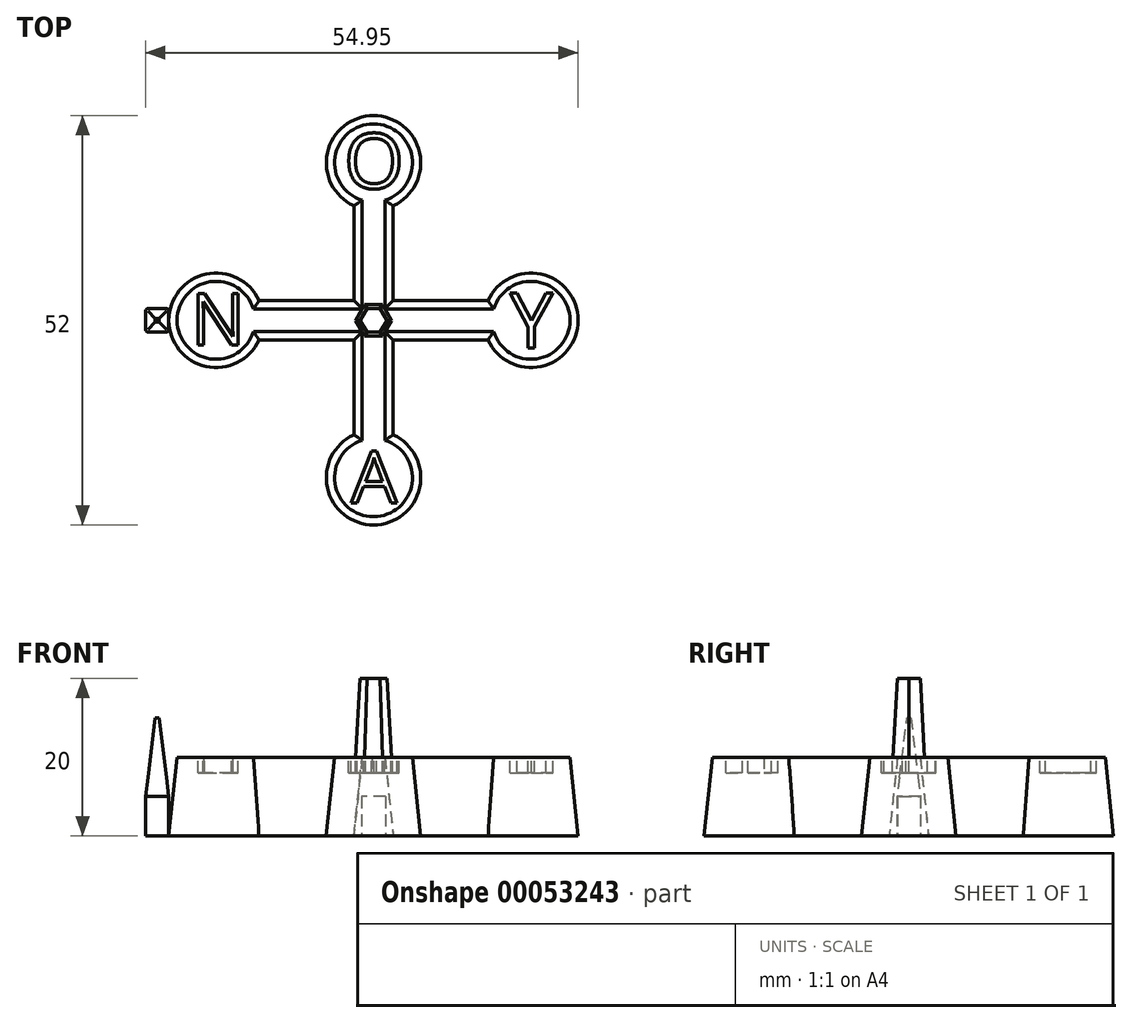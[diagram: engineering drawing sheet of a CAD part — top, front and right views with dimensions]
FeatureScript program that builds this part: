
annotation { "Feature Type Name" : "Feature", "Feature Type Description" : "" }
export const myFeature = defineFeature(function(context is Context, id is Id, definition is map)
    precondition{}
    {
        {
            var Q0;
            Q0=qCreatedBy(makeId("Top.planeOp"),FACE);
            var sketch = newSketch(context, id + "F0", { "sketchPlane" : qUnion([Q0])});
            skArc(sketch, "E0", {"start": v(-19.1, -5.93) * mm, "mid": v(20, 0) * mm, "end": v(-19.1, 5.93) * mm, "construction": true});
            skArc(sketch, "E1", {"start": v(2.5, 14.55) * mm, "mid": v(0, 26) * mm, "end": v(-2.5, 14.55) * mm});
            skArc(sketch, "E2", {"start": v(14.55, -2.5) * mm, "mid": v(26, 0) * mm, "end": v(14.55, 2.5) * mm});
            skArc(sketch, "E3", {"start": v(-2.5, -14.55) * mm, "mid": v(0, -26) * mm, "end": v(2.5, -14.55) * mm});
            skArc(sketch, "E4", {"start": v(-14.55, 2.5) * mm, "mid": v(-26, 0) * mm, "end": v(-14.55, -2.5) * mm});
            skLineSegment(sketch, "E5.rect.bottom", {"start": v(14.55, -2.5) * mm, "end": v(2.5, -2.5) * mm});
            skLineSegment(sketch, "E5.rect.top", {"start": v(14.55, 2.5) * mm, "end": v(2.5, 2.5) * mm});
            skLineSegment(sketch, "E6.rect.left", {"start": v(2.5, -14.55) * mm, "end": v(2.5, -2.5) * mm});
            skLineSegment(sketch, "E6.rect.right", {"start": v(-2.5, -14.55) * mm, "end": v(-2.5, -2.5) * mm});
            skLineSegment(sketch, "E7.trimOffspring", {"start": v(-2.5, 2.5) * mm, "end": v(-2.5, 14.55) * mm});
            skLineSegment(sketch, "E8.trimOffspring", {"start": v(-2.5, 2.5) * mm, "end": v(-14.55, 2.5) * mm});
            skLineSegment(sketch, "E9.trimOffspring", {"start": v(2.5, 2.5) * mm, "end": v(2.5, 14.55) * mm});
            skLineSegment(sketch, "E10.trimOffspring", {"start": v(-2.5, -2.5) * mm, "end": v(-14.55, -2.5) * mm});
            skSolve(sketch);
        }
        {
            var Q0;
            Q0 = qSketchRegion(id + "F0", true);
            extrude(context, id + "F1", {"entities" : qUnion([Q0]), "depth" : 10 * mm, "hasDraft" : true, "draftAngle" : 6 * degree, "draftPullDirection" : true});
        }
        {
            var Q0;
            Q0=makeQuery(id+"F1.opExtrude","CAP_FACE",FACE,{"disambiguationData":[OSD([sQuery(id+"F0.wireOp",EDGE,"E1"),sQuery(id+"F0.wireOp",EDGE,"E2"),sQuery(id+"F0.wireOp",EDGE,"E3"),sQuery(id+"F0.wireOp",EDGE,"E4"),sQuery(id+"F0.wireOp",EDGE,"E5.rect.bottom"),sQuery(id+"F0.wireOp",EDGE,"E5.rect.top"),sQuery(id+"F0.wireOp",EDGE,"E6.rect.left"),sQuery(id+"F0.wireOp",EDGE,"E6.rect.right"),sQuery(id+"F0.wireOp",EDGE,"E7.trimOffspring"),sQuery(id+"F0.wireOp",EDGE,"E8.trimOffspring"),sQuery(id+"F0.wireOp",EDGE,"E9.trimOffspring"),sQuery(id+"F0.wireOp",EDGE,"E10.trimOffspring")])],"isStart":false});
            var sketch = newSketch(context, id + "F2", { "sketchPlane" : qUnion([Q0])});
            skCircle(sketch, "E11.cCircle", {"center": v(0, 0) * mm, "radius": 2 * mm, "construction": true});
            skLineSegment(sketch, "E11.0", {"start": v(1.15, -2) * mm, "end": v(-1.15, -2) * mm});
            skLineSegment(sketch, "E11.1", {"start": v(-1.15, -2) * mm, "end": v(-2.3, 0) * mm});
            skLineSegment(sketch, "E11.2", {"start": v(-2.3, 0) * mm, "end": v(-1.15, 2) * mm});
            skLineSegment(sketch, "E11.3", {"start": v(-1.15, 2) * mm, "end": v(1.15, 2) * mm});
            skLineSegment(sketch, "E11.4", {"start": v(1.15, 2) * mm, "end": v(2.3, 0) * mm});
            skLineSegment(sketch, "E11.5", {"start": v(2.3, 0) * mm, "end": v(1.15, -2) * mm});
            skPoint(sketch, "E11.0.midPoint", {"position": v(0, -2) * mm});
            skSolve(sketch);
        }
        {
            var Q0;
            Q0 = qSketchRegion(id + "F2", true);
            extrude(context, id + "F3", {"entities" : qUnion([Q0]), "operationType" : NewBodyOperationType.ADD, "depth" : 10 * mm, "hasDraft" : true, "draftAngle" : 3 * degree, "draftPullDirection" : true});
        }
        {
            var Q0;
            Q0=makeQuery(id+"F1.opExtrude","CAP_FACE",FACE,{"disambiguationData":[OSD([sQuery(id+"F0.wireOp",EDGE,"E1"),sQuery(id+"F0.wireOp",EDGE,"E2"),sQuery(id+"F0.wireOp",EDGE,"E3"),sQuery(id+"F0.wireOp",EDGE,"E4"),sQuery(id+"F0.wireOp",EDGE,"E5.rect.bottom"),sQuery(id+"F0.wireOp",EDGE,"E5.rect.top"),sQuery(id+"F0.wireOp",EDGE,"E6.rect.left"),sQuery(id+"F0.wireOp",EDGE,"E6.rect.right"),sQuery(id+"F0.wireOp",EDGE,"E7.trimOffspring"),sQuery(id+"F0.wireOp",EDGE,"E8.trimOffspring"),sQuery(id+"F0.wireOp",EDGE,"E9.trimOffspring"),sQuery(id+"F0.wireOp",EDGE,"E10.trimOffspring")])],"isStart":true});
            var sketch = newSketch(context, id + "F4", { "sketchPlane" : qUnion([Q0])});
            skLineSegment(sketch, "E12.rect.bottom", {"start": v(1.5, -1.5) * mm, "end": v(-1.5, -1.5) * mm});
            skLineSegment(sketch, "E12.rect.top", {"start": v(1.5, 1.5) * mm, "end": v(-1.5, 1.5) * mm});
            skLineSegment(sketch, "E12.rect.left", {"start": v(1.5, -1.5) * mm, "end": v(1.5, 1.5) * mm});
            skLineSegment(sketch, "E12.rect.right", {"start": v(-1.5, -1.5) * mm, "end": v(-1.5, 1.5) * mm});
            skPoint(sketch, "E12.rect.middle", {"position": v(0, 0) * mm});
            skSolve(sketch);
        }
        {
            var Q0;
            Q0 = qSketchRegion(id + "F4", true);
            extrude(context, id + "F5", {"entities" : qUnion([Q0]), "operationType" : NewBodyOperationType.REMOVE, "oppositeDirection" : true, "depth" : 5 * mm});
        }
        {
            var Q0;
            Q0=qCreatedBy(makeId("Top.planeOp"),FACE);
            var sketch = newSketch(context, id + "F6", { "sketchPlane" : qUnion([Q0])});
            skLineSegment(sketch, "E13.rect.bottom", {"start": v(-26.3, -1.48) * mm, "end": v(-28.65, -1.48) * mm});
            skLineSegment(sketch, "E13.rect.top", {"start": v(-26.3, 1.47) * mm, "end": v(-28.65, 1.47) * mm});
            skLineSegment(sketch, "E13.rect.left", {"start": v(-26, -1.18) * mm, "end": v(-26, 1.17) * mm});
            skLineSegment(sketch, "E13.rect.right", {"start": v(-28.95, -1.18) * mm, "end": v(-28.95, 1.17) * mm});
            skPoint(sketch, "E13.rect.middle", {"position": v(-27.48, 0) * mm});
            skPoint(sketch, "E14.visualSharp", {"position": v(-28.95, 1.47) * mm});
            skArc(sketch, "E14.filletArc", {"start": v(-28.65, 1.47) * mm, "mid": v(-28.86, 1.39) * mm, "end": v(-28.95, 1.17) * mm});
            skPoint(sketch, "E15.visualSharp", {"position": v(-26, 1.47) * mm});
            skArc(sketch, "E15.filletArc", {"start": v(-26, 1.17) * mm, "mid": v(-26.09, 1.39) * mm, "end": v(-26.3, 1.47) * mm});
            skPoint(sketch, "E16.visualSharp", {"position": v(-26, -1.48) * mm});
            skArc(sketch, "E16.filletArc", {"start": v(-26.3, -1.48) * mm, "mid": v(-26.09, -1.39) * mm, "end": v(-26, -1.18) * mm});
            skPoint(sketch, "E17.visualSharp", {"position": v(-28.95, -1.48) * mm});
            skArc(sketch, "E17.filletArc", {"start": v(-28.95, -1.18) * mm, "mid": v(-28.86, -1.39) * mm, "end": v(-28.65, -1.48) * mm});
            skArc(sketch, "E18.0", {"start": v(-14.55, 2.5) * mm, "mid": v(-26, 0) * mm, "end": v(-14.55, -2.5) * mm, "construction": true});
            skSolve(sketch);
        }
        {
            var Q0;
            Q0=makeQuery(id+"F6.imprint","IMPRINT",FACE,{"disambiguationData":[TD([[makeQuery(id+"F6.imprint","IMPRINT",EDGE,{"derivedFrom":sQuery(id+"F6.wireOp",EDGE,"E13.rect.bottom")}),-1.0]])]});
            extrude(context, id + "F7", {"entities" : qUnion([Q0]), "operationType" : NewBodyOperationType.ADD, "depth" : 5 * mm});
        }
        {
            var Q0;
            Q0=makeQuery(id+"F7.opExtrude","CAP_FACE",FACE,{"disambiguationData":[OSD([sQuery(id+"F6.wireOp",EDGE,"E13.rect.bottom"),sQuery(id+"F6.wireOp",EDGE,"E13.rect.top"),sQuery(id+"F6.wireOp",EDGE,"E13.rect.left"),sQuery(id+"F6.wireOp",EDGE,"E13.rect.right"),sQuery(id+"F6.wireOp",EDGE,"E14.filletArc"),sQuery(id+"F6.wireOp",EDGE,"E15.filletArc"),sQuery(id+"F6.wireOp",EDGE,"E16.filletArc"),sQuery(id+"F6.wireOp",EDGE,"E17.filletArc")])],"isStart":false});
            extrude(context, id + "F8", {"entities" : qUnion([Q0]), "operationType" : NewBodyOperationType.ADD, "depth" : 10 * mm, "hasDraft" : true, "draftAngle" : 7 * degree, "draftPullDirection" : true});
        }
        {
            var Q0;
            {var subQ2=sQuery(id+"F0.wireOp",EDGE,"E10.trimOffspring");var subQ3=sQuery(id+"F0.wireOp",EDGE,"E8.trimOffspring");var subQ4=sQuery(id+"F0.wireOp",EDGE,"E4");Q0=makeQuery(id+"F3.boolean.opBoolean","SPLIT",FACE,{"disambiguationData":[TD([makeQuery(id+"F1.opExtrude","SWEPT_FACE",FACE,{"disambiguationData":[OSD([subQ4])]})])],"derivedFrom":makeQuery(id+"F1.opExtrude","CAP_FACE",FACE,{"disambiguationData":[OSD([sQuery(id+"F0.wireOp",EDGE,"E1"),sQuery(id+"F0.wireOp",EDGE,"E2"),sQuery(id+"F0.wireOp",EDGE,"E3"),subQ4,sQuery(id+"F0.wireOp",EDGE,"E5.rect.bottom"),sQuery(id+"F0.wireOp",EDGE,"E5.rect.top"),sQuery(id+"F0.wireOp",EDGE,"E6.rect.left"),sQuery(id+"F0.wireOp",EDGE,"E6.rect.right"),sQuery(id+"F0.wireOp",EDGE,"E7.trimOffspring"),subQ3,sQuery(id+"F0.wireOp",EDGE,"E9.trimOffspring"),subQ2])],"isStart":false})});}
            var sketch = newSketch(context, id + "F9", { "sketchPlane" : qUnion([Q0])});
            skText(sketch, "E19", { "text": "O", "fontName": "OpenSans-Regular.ttf"});
            skText(sketch, "E20", { "text": "A", "fontName": "OpenSans-Regular.ttf"});
            skText(sketch, "E21", { "text": "N", "fontName": "OpenSans-Regular.ttf"});
            skText(sketch, "E22", { "text": "Y", "fontName": "OpenSans-Regular.ttf"});
            const initialGuessF9  = {"E19": [-0.00374, 0.01675, 1, 0, 0.00702], "E20": [-0.00285, -0.02323, 1, 0, 0.00664], "E21": [-0.0232, -0.00314, 1, 0, 0.0066], "E22": [0.01732, -0.0035, 1, 0, 0.00703]};
            skSetInitialGuess(sketch, initialGuessF9);
            skSolve(sketch);
        }
        {
            var Q0;
            Q0 = qSketchRegion(id + "F9", true);
            extrude(context, id + "F10", {"entities" : qUnion([Q0]), "operationType" : NewBodyOperationType.REMOVE, "oppositeDirection" : true, "depth" : 2 * mm});
        }
    });
